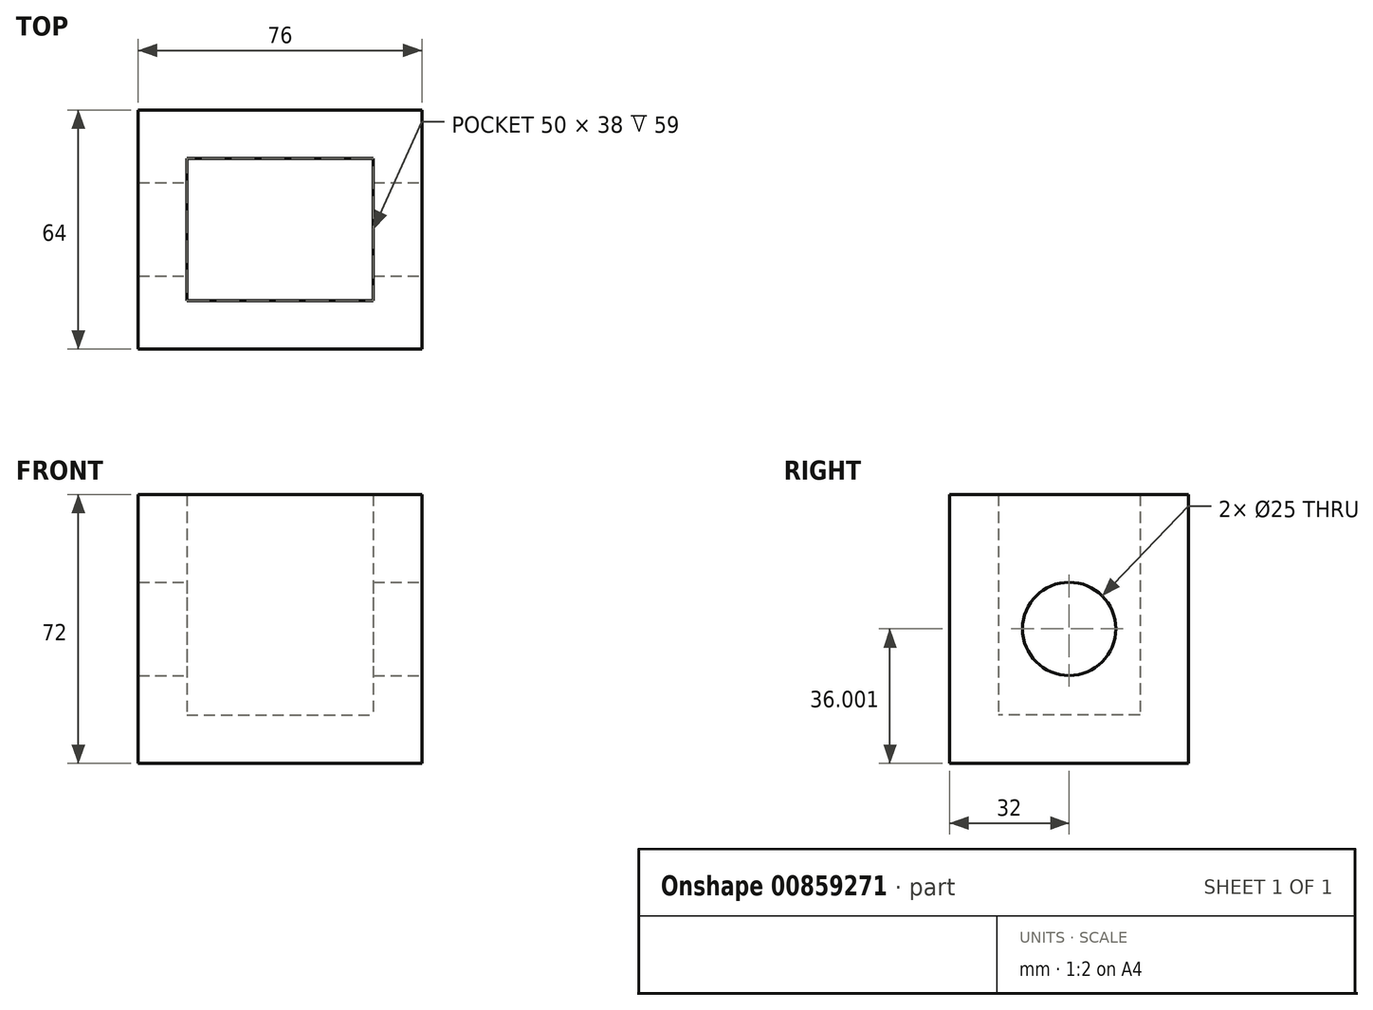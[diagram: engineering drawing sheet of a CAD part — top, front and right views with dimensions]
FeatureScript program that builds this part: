
annotation { "Feature Type Name" : "Feature", "Feature Type Description" : "" }
export const myFeature = defineFeature(function(context is Context, id is Id, definition is map)
    precondition{}
    {
        {
            var Q0;
            Q0=qCreatedBy(makeId("Front.planeOp"),FACE);
            var sketch = newSketch(context, id + "F0", { "sketchPlane" : qUnion([Q0])});
            skLineSegment(sketch, "E0.bottom", {"start": v(-36.56, 40.84) * mm, "end": v(39.44, 40.84) * mm});
            skLineSegment(sketch, "E0.top", {"start": v(-36.56, -31.16) * mm, "end": v(39.44, -31.16) * mm});
            skLineSegment(sketch, "E0.left", {"start": v(-36.56, 40.84) * mm, "end": v(-36.56, -31.16) * mm});
            skLineSegment(sketch, "E0.right", {"start": v(39.44, 40.84) * mm, "end": v(39.44, -31.16) * mm});
            skLineSegment(sketch, "E1", {"start": v(-36.56, -13.16) * mm, "end": v(39.44, -13.16) * mm});
            skSolve(sketch);
        }
        {
            var Q0;
            {var subQ0=sQuery(id+"F0.wireOp",EDGE,"E0.bottom");Q0=makeQuery(id+"F0.imprint","IMPRINT",FACE,{"disambiguationData":[TD([[makeQuery(id+"F0.imprint","IMPRINT",EDGE,{"derivedFrom":subQ0}),-1.0]])]});}
            var Q1;
            {var subQ0=sQuery(id+"F0.wireOp",EDGE,"E0.top");Q1=makeQuery(id+"F0.imprint","IMPRINT",FACE,{"disambiguationData":[TD([[makeQuery(id+"F0.imprint","IMPRINT",EDGE,{"derivedFrom":subQ0}),1.0]])]});}
            extrude(context, id + "F1", {"entities" : qUnion([Q0, Q1]), "oppositeDirection" : true, "depth" : 64 * mm, "offsetDistance" : 25 * mm});
        }
        {
            var Q0;
            Q0=makeQuery(id+"F1.opExtrude","SWEPT_FACE",FACE,{"disambiguationData":[OSD([sQuery(id+"F0.wireOp",EDGE,"E0.bottom")])]});
            shell(context, id + "F2", {"entities" : qUnion([Q0]), "thickness" : 13 * mm});
        }
        {
            var Q0;
            Q0=makeQuery(id+"F1.opExtrude","SWEPT_FACE",FACE,{"disambiguationData":[OSD([sQuery(id+"F0.wireOp",EDGE,"E0.right")])]});
            var sketch = newSketch(context, id + "F3", { "sketchPlane" : qUnion([Q0])});
            skCircle(sketch, "E2", {"center": v(32, 4.84) * mm, "radius": 12.5 * mm});
            skSolve(sketch);
        }
        {
            var Q0;
            Q0=makeQuery(id+"F3.imprint","IMPRINT",FACE,{"disambiguationData":[TD([[makeQuery(id+"F3.imprint","IMPRINT",EDGE,{"derivedFrom":sQuery(id+"F3.wireOp",EDGE,"E2")}),1.0]])]});
            extrude(context, id + "F4", {"entities" : qUnion([Q0]), "operationType" : NewBodyOperationType.REMOVE, "oppositeDirection" : true, "depth" : 103.3 * mm, "offsetDistance" : 25 * mm});
        }
    });
